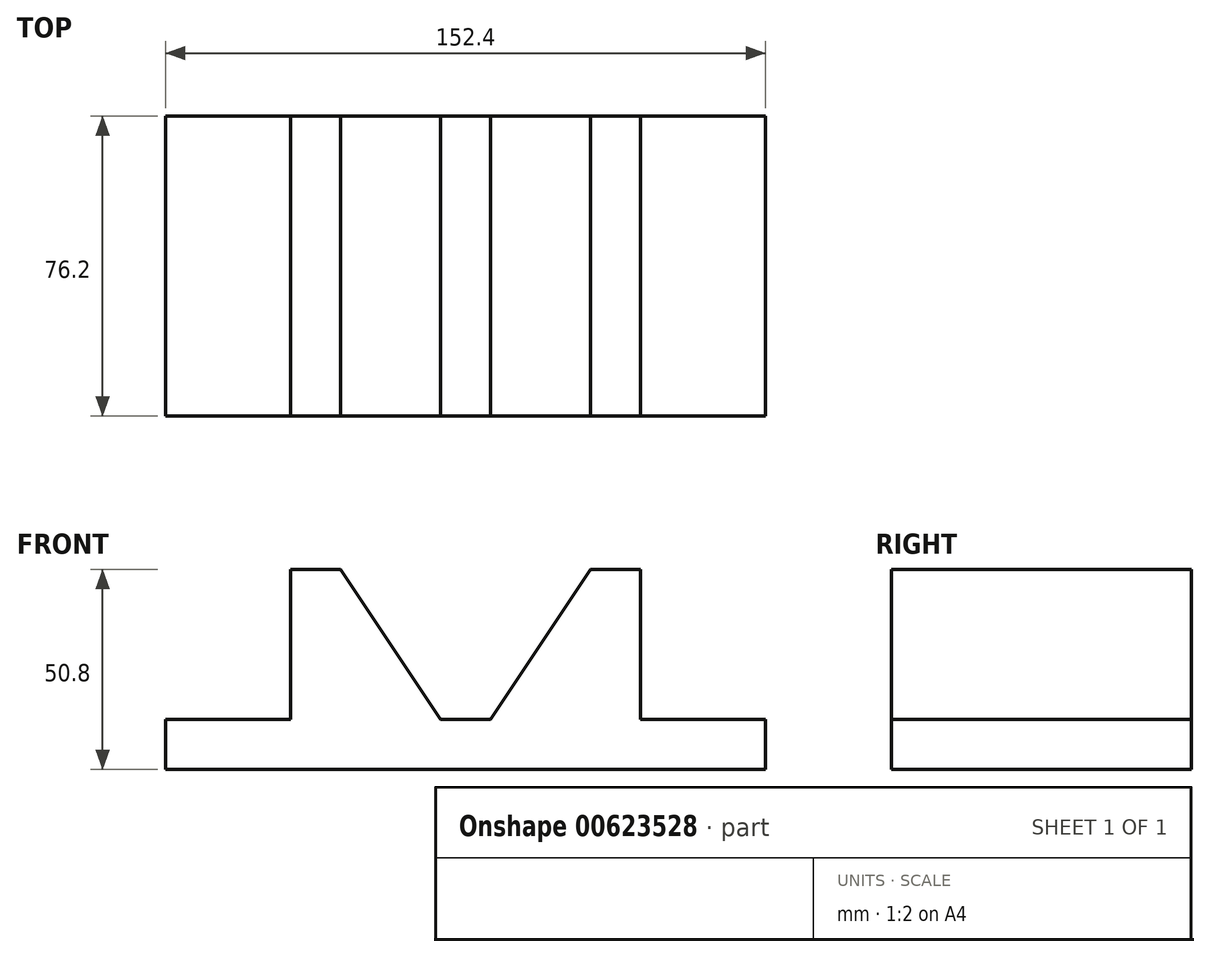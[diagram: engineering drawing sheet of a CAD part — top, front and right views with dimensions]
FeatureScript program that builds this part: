
annotation { "Feature Type Name" : "Feature", "Feature Type Description" : "" }
export const myFeature = defineFeature(function(context is Context, id is Id, definition is map)
    precondition{}
    {
        {
            var Q0;
            Q0=qCreatedBy(makeId("Front.planeOp"),FACE);
            var sketch = newSketch(context, id + "F0", { "sketchPlane" : qUnion([Q0])});
            skLineSegment(sketch, "E0", {"start": v(0, 0) * mm, "end": v(152.4, 0) * mm});
            skLineSegment(sketch, "E1", {"start": v(0, 0) * mm, "end": v(0, 12.7) * mm});
            skLineSegment(sketch, "E2", {"start": v(152.4, 0) * mm, "end": v(152.4, 12.7) * mm});
            skLineSegment(sketch, "E3", {"start": v(0, 12.7) * mm, "end": v(31.75, 12.7) * mm});
            skLineSegment(sketch, "E4", {"start": v(152.4, 12.7) * mm, "end": v(120.65, 12.7) * mm});
            skLineSegment(sketch, "E5", {"start": v(31.75, 12.7) * mm, "end": v(31.75, 50.8) * mm});
            skLineSegment(sketch, "E6", {"start": v(120.65, 12.7) * mm, "end": v(120.65, 50.8) * mm});
            skLineSegment(sketch, "E7", {"start": v(31.75, 50.8) * mm, "end": v(44.45, 50.8) * mm});
            skLineSegment(sketch, "E8", {"start": v(120.65, 50.8) * mm, "end": v(107.95, 50.8) * mm});
            skLineSegment(sketch, "E9", {"start": v(0, 0) * mm, "end": v(69.85, 0) * mm});
            skLineSegment(sketch, "E10", {"start": v(44.45, 50.8) * mm, "end": v(69.85, 12.7) * mm});
            skLineSegment(sketch, "E11", {"start": v(69.85, 0) * mm, "end": v(82.55, 0) * mm});
            skLineSegment(sketch, "E12", {"start": v(82.55, 12.7) * mm, "end": v(107.95, 50.8) * mm});
            skLineSegment(sketch, "E13", {"start": v(69.85, 12.7) * mm, "end": v(82.55, 12.7) * mm});
            skSolve(sketch);
        }
        {
            var Q0;
            Q0 = qSketchRegion(id + "F0", true);
            extrude(context, id + "F1", {"entities" : qUnion([Q0]), "depth" : 76.2 * mm, "offsetDistance" : 25.4 * mm});
        }
    });
